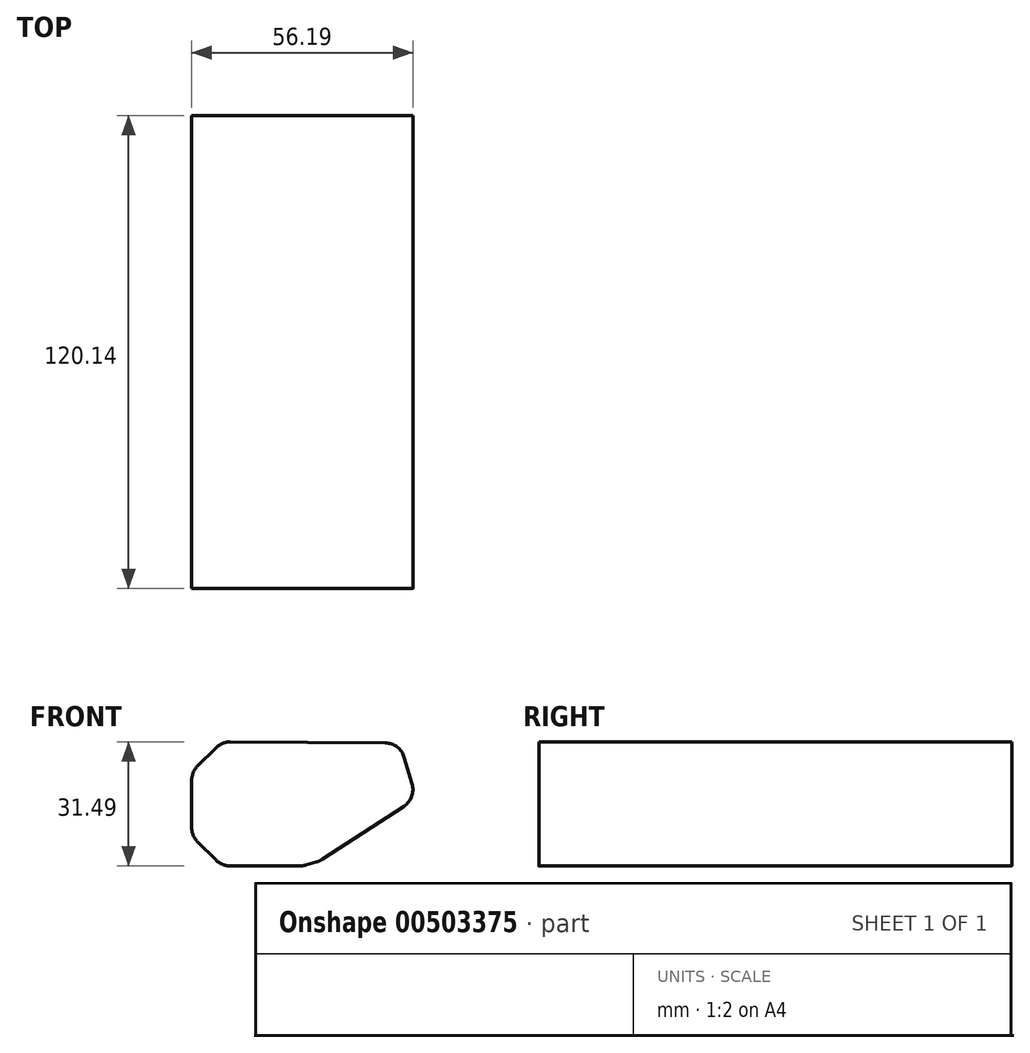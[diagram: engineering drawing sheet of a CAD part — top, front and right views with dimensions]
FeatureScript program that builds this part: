
annotation { "Feature Type Name" : "Feature", "Feature Type Description" : "" }
export const myFeature = defineFeature(function(context is Context, id is Id, definition is map)
    precondition{}
    {
        {
            var Q0;
            Q0=qCreatedBy(makeId("Front.planeOp"),FACE);
            var sketch = newSketch(context, id + "F0", { "sketchPlane" : qUnion([Q0])});
            skLineSegment(sketch, "E0", {"start": v(-30.59, 31.55) * mm, "end": v(-30.59, 0) * mm});
            skLineSegment(sketch, "E1", {"start": v(-30.59, 0) * mm, "end": v(0, 0) * mm});
            skLineSegment(sketch, "E2", {"start": v(0, 0) * mm, "end": v(47.74, 31.08) * mm});
            skLineSegment(sketch, "E3", {"start": v(47.74, 31.08) * mm, "end": v(-30.59, 31.55) * mm});
            skSolve(sketch);
        }
        {
            var Q0;
            Q0=sQuery(id+"F0.wireOp",EDGE,"E0");
            var Q1;
            Q1=sQuery(id+"F0.wireOp",EDGE,"E1");
            var Q2;
            Q2=sQuery(id+"F0.wireOp",EDGE,"E2");
            var Q3;
            Q3=sQuery(id+"F0.wireOp",EDGE,"E3");
            extrude(context, id + "F1", {"bodyType" : ToolBodyType.SURFACE, "surfaceEntities" : qUnion([Q0, Q1, Q2, Q3]), "depth" : 120.14 * mm});
        }
        {
            var Q0;
            Q0=makeQuery(id+"F1.opExtrude","SWEPT_FACE",FACE,{"disambiguationData":[OSD([sQuery(id+"F0.wireOp",EDGE,"E0")])]});
            var Q1;
            Q1=makeQuery(id+"F1.opExtrude","SWEPT_FACE",FACE,{"disambiguationData":[OSD([sQuery(id+"F0.wireOp",EDGE,"E2")])]});
            var Q2;
            Q2=makeQuery(id+"F1.opExtrude","SWEPT_FACE",FACE,{"disambiguationData":[OSD([sQuery(id+"F0.wireOp",EDGE,"E1")])]});
            var Q3;
            Q3=makeQuery(id+"F1.opExtrude","SWEPT_EDGE",EDGE,{"disambiguationData":[OSD([sQuery(id+"F0.wireOp",VERTEX,"E2.start")])]});
            chamfer(context, id + "F2", {"entities" : qUnion([Q0, Q1, Q2, Q3]), "width" : 7.62 * mm, "tangentPropagation" : true});
        }
        {
            var Q0;
            Q0=makeQuery(id+"F1.opExtrude","SWEPT_FACE",FACE,{"disambiguationData":[OSD([sQuery(id+"F0.wireOp",EDGE,"E1")])]});
            var Q1;
            Q1=makeQuery(id+"F1.opExtrude","SWEPT_FACE",FACE,{"disambiguationData":[OSD([sQuery(id+"F0.wireOp",EDGE,"E0")])]});
            var Q2;
            Q2=makeQuery(id+"F1.opExtrude","SWEPT_FACE",FACE,{"disambiguationData":[OSD([sQuery(id+"F0.wireOp",EDGE,"E3")])]});
            var Q3;
            Q3=makeQuery(id+"F1.opExtrude","SWEPT_FACE",FACE,{"disambiguationData":[OSD([sQuery(id+"F0.wireOp",EDGE,"E2")])]});
            fillet(context, id + "F3", {"entities" : qUnion([Q0, Q1, Q2, Q3]), "radius" : 5.08 * mm, "tangentPropagation" : true, "allowEdgeOverflow" : false});
        }
    });
